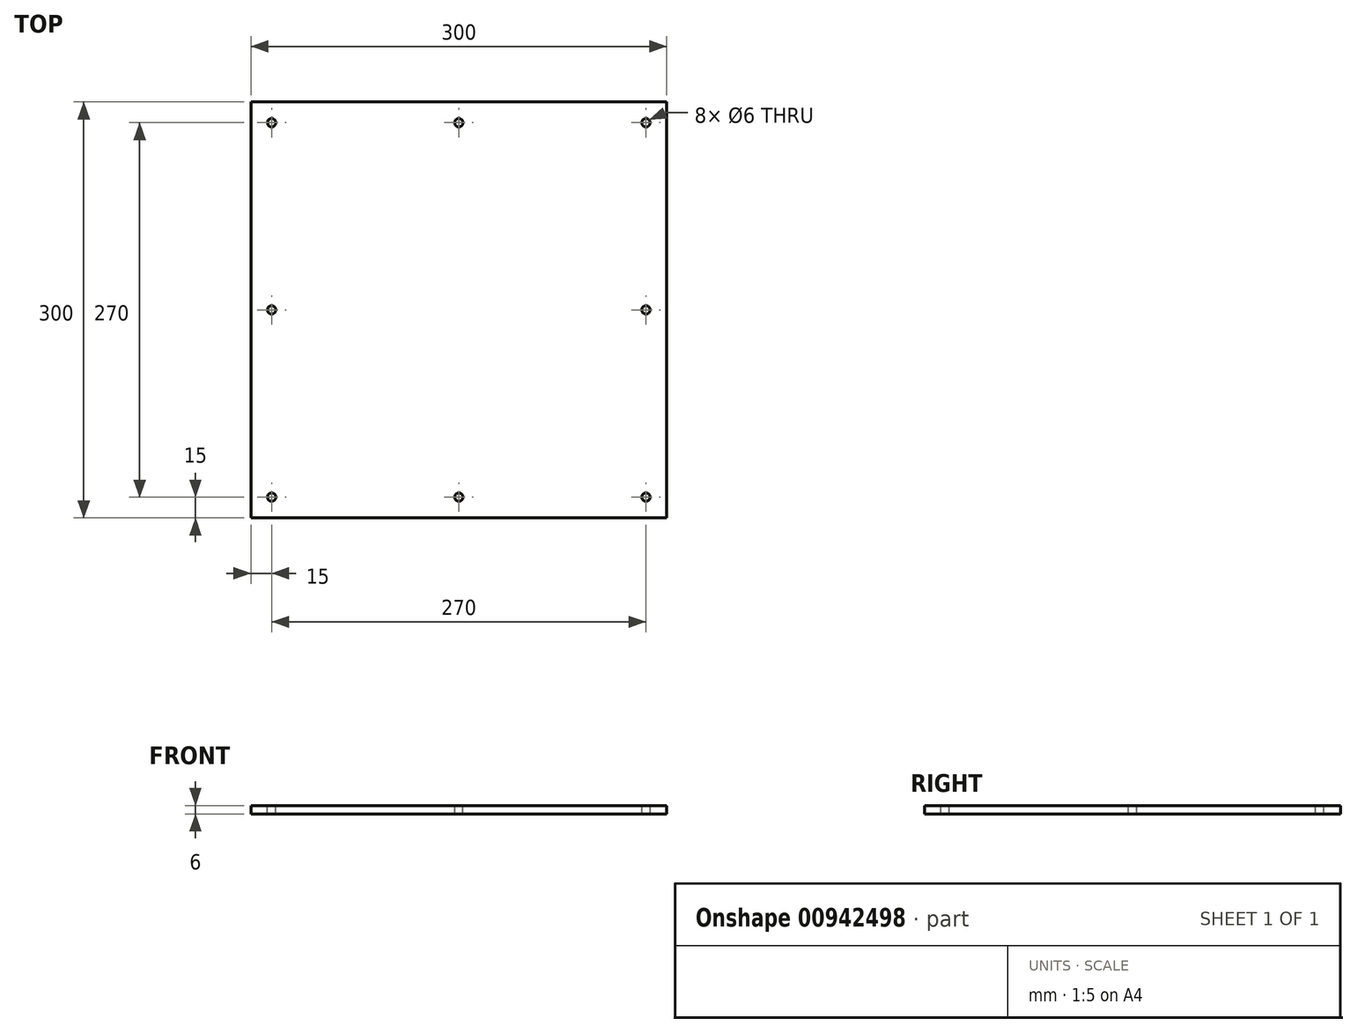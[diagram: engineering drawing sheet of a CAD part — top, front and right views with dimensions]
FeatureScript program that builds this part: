
annotation { "Feature Type Name" : "Feature", "Feature Type Description" : "" }
export const myFeature = defineFeature(function(context is Context, id is Id, definition is map)
    precondition{}
    {
        {
            var Q0;
            Q0=qCreatedBy(makeId("Top.planeOp"),FACE);
            var sketch = newSketch(context, id + "F0", { "sketchPlane" : qUnion([Q0])});
            skLineSegment(sketch, "E0.bottom", {"start": v(0, 0) * mm, "end": v(300, 0) * mm});
            skLineSegment(sketch, "E0.top", {"start": v(0, -300) * mm, "end": v(300, -300) * mm});
            skLineSegment(sketch, "E0.left", {"start": v(0, 0) * mm, "end": v(0, -300) * mm});
            skLineSegment(sketch, "E0.right", {"start": v(300, 0) * mm, "end": v(300, -300) * mm});
            skSolve(sketch);
        }
        {
            var Q0;
            Q0 = qSketchRegion(id + "F0", true);
            extrude(context, id + "F1", {"entities" : qUnion([Q0]), "depth" : 6 * mm, "offsetDistance" : 25 * mm});
        }
        {
            var Q0;
            Q0=makeQuery(id+"F1.opExtrude","CAP_FACE",FACE,{"disambiguationData":[OSD([sQuery(id+"F0.wireOp",EDGE,"E0.bottom"),sQuery(id+"F0.wireOp",EDGE,"E0.top"),sQuery(id+"F0.wireOp",EDGE,"E0.left"),sQuery(id+"F0.wireOp",EDGE,"E0.right")])],"isStart":false});
            var sketch = newSketch(context, id + "F2", { "sketchPlane" : qUnion([Q0])});
            skLineSegment(sketch, "E1.0", {"start": v(15, -15) * mm, "end": v(285, -15) * mm, "construction": true});
            skLineSegment(sketch, "E1.1", {"start": v(15, -15) * mm, "end": v(15, -285) * mm, "construction": true});
            skLineSegment(sketch, "E1.2", {"start": v(15, -285) * mm, "end": v(285, -285) * mm, "construction": true});
            skLineSegment(sketch, "E1.3", {"start": v(285, -15) * mm, "end": v(285, -285) * mm, "construction": true});
            skCircle(sketch, "E2", {"center": v(15, -15) * mm, "radius": 3 * mm});
            skCircle(sketch, "E3", {"center": v(285, -15) * mm, "radius": 3 * mm});
            skCircle(sketch, "E4", {"center": v(285, -285) * mm, "radius": 3 * mm});
            skCircle(sketch, "E5", {"center": v(15, -285) * mm, "radius": 3 * mm});
            skCircle(sketch, "E6", {"center": v(150, -285) * mm, "radius": 3 * mm});
            skCircle(sketch, "E7", {"center": v(15, -150) * mm, "radius": 3 * mm});
            skCircle(sketch, "E8", {"center": v(285, -150) * mm, "radius": 3 * mm});
            skCircle(sketch, "E9", {"center": v(150, -15) * mm, "radius": 3 * mm});
            skSolve(sketch);
        }
        {
            var Q0;
            Q0 = qSketchRegion(id + "F2", true);
            extrude(context, id + "F3", {"entities" : qUnion([Q0]), "operationType" : NewBodyOperationType.REMOVE, "oppositeDirection" : true, "depth" : 25 * mm, "offsetDistance" : 25 * mm});
        }
    });
